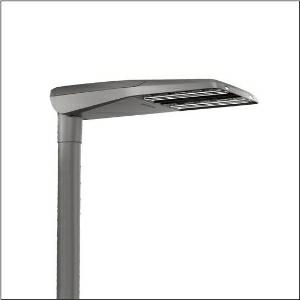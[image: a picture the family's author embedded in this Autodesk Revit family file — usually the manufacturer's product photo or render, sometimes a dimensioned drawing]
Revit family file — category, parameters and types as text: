
# Revit family: streetlight_sl_11_iq_midi___pc-l_5xc3e51e08me_2942
name_source: partatom
category: Lighting Fixtures
units: mm (PartAtom-declared; Revit-internal decimal feet)

## family parameters
Cut with Voids When Loaded = No
Host = Face
Light Source = No
Part Type = Normal
Room Calculation Point = No
Round Connector Dimension = Use Diameter
Shared = No

## types (1)
- --- (1 x LED, 15540 lm, 124.7 W, 3000K)
    Apparent Load = 125 VA
    CIE Flux Codes = 37 73 96 100 100
    Color Rendering = 70
    Color Temperature = 3000K
    Default Elevation = 1800 mm
    Description = Streetlight SL 11 iQ midi, mast luminaire, primary light control with 3 zone facetted reflector, of plastic, silver coated, highly specular, primary optical cover: cover, of PMMA, transparent, light distribution: PC-L, light emission: direct distribution, primary light characteristic: asymmetric, installation type: post-top, side-entry, LED, High Power LED, rated luminous flux: 15.540lm, luminous efficacy: 125lm/W, light colour: 730, colour temperature: 3000K, control: optimised constant luminous flux control (CLO 2.0), Desk-Remote (wireless, voltage-free reading and setting of iQ features in the workshop via application-optimized NFC function/RFID function), Light-Fading, Smart-Wire, Night-Set, Lumen-Switch, Temp-Guard, Auto-Match, with cable H07RN-F 5x 1.5mm², mains connection: 220..240V, AC, 50/60Hz, connection cable pre-assembled, cable length: 12,5m, start of lifetime: 125W, end of lifetime: 132W, reduction: 61W, luminaire housing, of diecast aluminium, powder-coated, Siteco® metallic grey (DB 702S), length: 780mm, width: 376mm, height: 118mm, spigot size: 60/76mm (post-top) and 42/60/76mm (side-entry), mast flange for spigot size: 42mm: 5XC10008XM4, 60mm: 5XC10008XM2, 76/60mm: 5XC10108XM1, equipment: Power, protection rating (complete): IP66, insulation class (complete): insulation class II (safety insulation), certification: CE, ENEC, VDE, impact resistance: IK09, permissible operating ambient temperature for outdoor applications: -25..+50°C, standard-compliant lighting for roads and squares, packaging unit: 1 piece

Light Distribution: PC-L
    Height = 118 mm
    Lamp = 1 x LED
    Lamp Light Flux = 15540 lm
    Lamp Power = 124.7 W
    Lamp count = 1
    Length = 780 mm
    Luminous efficacy = 125 lm/W
    Manufacturer = Siteco
    ModVariant = No
    Model = 5XC3E51E08ME
    Number of Poles = 1
    OnlyDefault = Yes
    Power Factor = 1
    Product Name = Streetlight SL 11 iQ midi | PC-L
    Product group = mast luminaire | pylon top
    ProductGroupID = 6100
    Protection Class = Protection class II
    Protection Degree = IP 66
    RLX_Detail_Level = 1
    RlxData = <blob elided: 74437 chars, md5=97e8d896>
    Socket = socket
    Standby Power = 0 W
    System Light Flux = 15540 lm
    System Power = 125 W
    Type Comments = factory setting: luminous flux: 100 % | dim-lin: 254 | 557 mA
    Type Image = l_1005960.jpg
    URL = http://relux.com
    VarID = @adj_117969
    Voltage = 0 V
    Weight = 0.00 kg
    Width = 376 mm

## geometry (parser evidence)
native form markers: Blend x4, Sweep x10
no freeform markers — native parametric forms only
